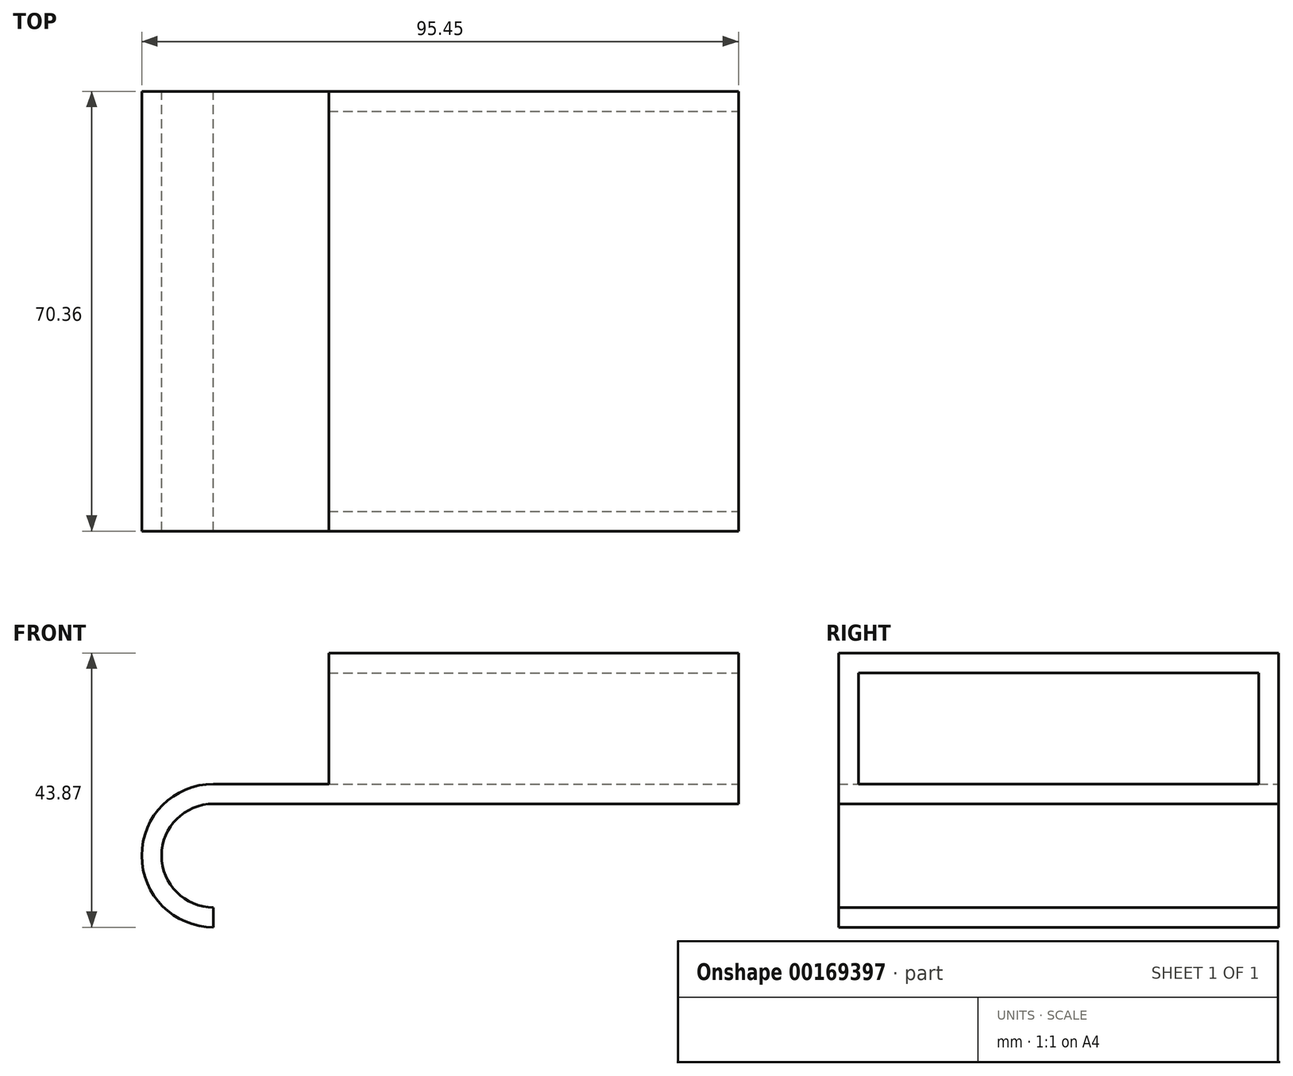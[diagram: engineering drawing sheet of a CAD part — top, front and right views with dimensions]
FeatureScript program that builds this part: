
annotation { "Feature Type Name" : "Feature", "Feature Type Description" : "" }
export const myFeature = defineFeature(function(context is Context, id is Id, definition is map)
    precondition{}
    {
        {
            var Q0;
            Q0=qCreatedBy(makeId("Front.planeOp"),FACE);
            var sketch = newSketch(context, id + "F0", { "sketchPlane" : qUnion([Q0])});
            skLineSegment(sketch, "E0", {"start": v(0, -3.18) * mm, "end": v(84, -3.18) * mm});
            skLineSegment(sketch, "E1", {"start": v(84, -3.18) * mm, "end": v(84, 0) * mm});
            skLineSegment(sketch, "E2", {"start": v(84, 0) * mm, "end": v(0, 0) * mm});
            skLineSegment(sketch, "E3", {"start": v(0, -19.73) * mm, "end": v(0, -22.9) * mm});
            skArc(sketch, "E4", {"start": v(0, -3.17) * mm, "mid": v(-8.28, -11.45) * mm, "end": v(0, -19.73) * mm});
            skArc(sketch, "E5", {"start": v(0, 0) * mm, "mid": v(-11.45, -11.45) * mm, "end": v(0, -22.9) * mm});
            skSolve(sketch);
        }
        {
            var Q0;
            Q0=makeQuery(id+"F0.imprint","IMPRINT",FACE,{"disambiguationData":[TD([[makeQuery(id+"F0.imprint","IMPRINT",EDGE,{"derivedFrom":sQuery(id+"F0.wireOp",EDGE,"E0")}),1.0]])]});
            extrude(context, id + "F1", {"entities" : qUnion([Q0]), "depth" : 70.36 * mm});
        }
        {
            var Q0;
            Q0=makeQuery(id+"F1.opExtrude","SWEPT_FACE",FACE,{"disambiguationData":[OSD([sQuery(id+"F0.wireOp",EDGE,"E1")])]});
            var sketch = newSketch(context, id + "F2", { "sketchPlane" : qUnion([Q0])});
            skLineSegment(sketch, "E6.bottom", {"start": v(-70.36, 0) * mm, "end": v(0, 0) * mm});
            skLineSegment(sketch, "E6.top", {"start": v(-70.36, 20.96) * mm, "end": v(0, 20.96) * mm});
            skLineSegment(sketch, "E6.left", {"start": v(-70.36, 0) * mm, "end": v(-70.36, 20.96) * mm});
            skLineSegment(sketch, "E6.right", {"start": v(0, 0) * mm, "end": v(0, 20.96) * mm});
            skSolve(sketch);
        }
        {
            var Q0;
            Q0=makeQuery(id+"F2.imprint","IMPRINT",FACE,{"disambiguationData":[TD([[makeQuery(id+"F2.imprint","IMPRINT",EDGE,{"derivedFrom":sQuery(id+"F2.wireOp",EDGE,"E6.bottom")}),1.0]])]});
            extrude(context, id + "F3", {"entities" : qUnion([Q0]), "operationType" : NewBodyOperationType.ADD, "oppositeDirection" : true, "depth" : 65.53 * mm});
        }
        {
            var Q0;
            Q0=makeQuery(id+"F3.boolean.opBoolean","MERGE",FACE,{"derivedFrom":[makeQuery(id+"F1.opExtrude","SWEPT_FACE",FACE,{"disambiguationData":[OSD([sQuery(id+"F0.wireOp",EDGE,"E1")])]}),makeQuery(id+"F3.opExtrude","CAP_FACE",FACE,{"disambiguationData":[OSD([sQuery(id+"F2.wireOp",EDGE,"E6.bottom"),sQuery(id+"F2.wireOp",EDGE,"E6.top"),sQuery(id+"F2.wireOp",EDGE,"E6.left"),sQuery(id+"F2.wireOp",EDGE,"E6.right")])],"isStart":true})]});
            var sketch = newSketch(context, id + "F4", { "sketchPlane" : qUnion([Q0])});
            skLineSegment(sketch, "E7.bottom", {"start": v(-67.18, 0) * mm, "end": v(-3.18, 0) * mm});
            skLineSegment(sketch, "E7.top", {"start": v(-67.18, 17.78) * mm, "end": v(-3.17, 17.78) * mm});
            skLineSegment(sketch, "E7.left", {"start": v(-67.18, 0) * mm, "end": v(-67.18, 17.78) * mm});
            skLineSegment(sketch, "E7.right", {"start": v(-3.17, 0) * mm, "end": v(-3.17, 17.78) * mm});
            skSolve(sketch);
        }
        {
            var Q0;
            Q0=makeQuery(id+"F4.imprint","IMPRINT",FACE,{"disambiguationData":[TD([[makeQuery(id+"F4.imprint","IMPRINT",EDGE,{"derivedFrom":sQuery(id+"F4.wireOp",EDGE,"E7.bottom")}),1.0]])]});
            extrude(context, id + "F5", {"entities" : qUnion([Q0]), "operationType" : NewBodyOperationType.REMOVE, "oppositeDirection" : true, "depth" : 93.47 * mm});
        }
    });
